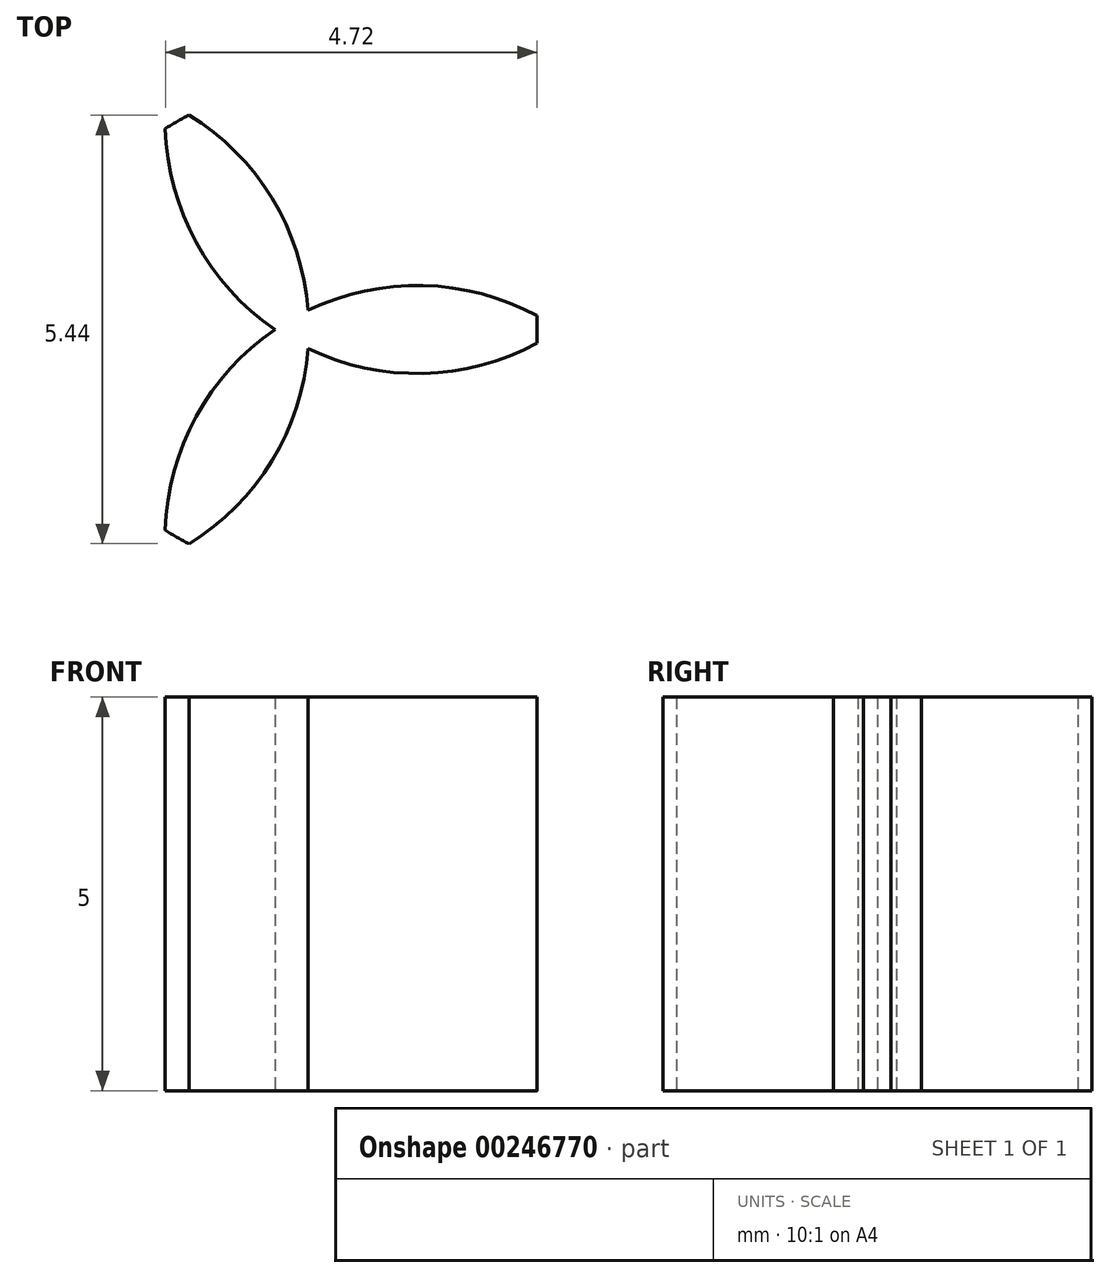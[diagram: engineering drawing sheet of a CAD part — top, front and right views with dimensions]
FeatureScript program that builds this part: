
annotation { "Feature Type Name" : "Feature", "Feature Type Description" : "" }
export const myFeature = defineFeature(function(context is Context, id is Id, definition is map)
    precondition{}
    {
        {
            var Q0;
            Q0=qCreatedBy(makeId("Top.planeOp"),FACE);
            var sketch = newSketch(context, id + "F0", { "sketchPlane" : qUnion([Q0])});
            skCircle(sketch, "E0", {"center": v(0, 0) * mm, "radius": 3.05 * mm});
            skArc(sketch, "E1.cCircle", {"start": v(-1.37, -2.72) * mm, "mid": v(3.05, 0) * mm, "end": v(-1.37, 2.72) * mm, "construction": true});
            skCircle(sketch, "E2", {"center": v(-3.05, 0) * mm, "radius": 3.2 * mm});
            skCircle(sketch, "E3.1.0", {"center": v(1.52, -2.64) * mm, "radius": 3.2 * mm});
            skCircle(sketch, "E3.2.0", {"center": v(1.53, 2.64) * mm, "radius": 3.2 * mm});
            skPoint(sketch, "E1.0.start.orphan", {"position": v(3.05, 0) * mm});
            skSolve(sketch);
        }
        {
            var Q0;
            {var subQ0=sQuery(id+"F0.wireOp",EDGE,"E2");var subQ1=sQuery(id+"F0.wireOp",EDGE,"E0");var subQ2=makeQuery(id+"F0.imprint","INTERSECT",VERTEX,{"disambiguationData":[OD(0.0)],"derivedFrom":[subQ1,subQ0]});Q0=makeQuery(id+"F0.imprint","IMPRINT",FACE,{"disambiguationData":[TD([[makeQuery(id+"F0.imprint","IMPRINT",EDGE,{"disambiguationData":[TD([[subQ2,-1.0]])],"derivedFrom":subQ1}),1.0]])]});}
            var Q1;
            {var subQ0=sQuery(id+"F0.wireOp",EDGE,"E3.1.0");var subQ1=sQuery(id+"F0.wireOp",EDGE,"E0");var subQ2=makeQuery(id+"F0.imprint","INTERSECT",VERTEX,{"disambiguationData":[OD(1.0)],"derivedFrom":[subQ1,subQ0]});Q1=makeQuery(id+"F0.imprint","IMPRINT",FACE,{"disambiguationData":[TD([[makeQuery(id+"F0.imprint","IMPRINT",EDGE,{"disambiguationData":[TD([[subQ2,-1.0]])],"derivedFrom":subQ1}),1.0]])]});}
            var Q2;
            {var subQ0=sQuery(id+"F0.wireOp",EDGE,"E3.1.0");var subQ1=sQuery(id+"F0.wireOp",EDGE,"E0");var subQ2=makeQuery(id+"F0.imprint","INTERSECT",VERTEX,{"disambiguationData":[OD(0.0)],"derivedFrom":[subQ1,subQ0]});Q2=makeQuery(id+"F0.imprint","IMPRINT",FACE,{"disambiguationData":[TD([[makeQuery(id+"F0.imprint","IMPRINT",EDGE,{"disambiguationData":[TD([[subQ2,1.0]])],"derivedFrom":subQ1}),1.0]])]});}
            var Q3;
            {var subQ0=sQuery(id+"F0.wireOp",EDGE,"E3.1.0");var subQ1=sQuery(id+"F0.wireOp",EDGE,"E2");var subQ2=makeQuery(id+"F0.imprint","INTERSECT",VERTEX,{"disambiguationData":[OD(1.0)],"derivedFrom":[subQ1,subQ0]});Q3=makeQuery(id+"F0.imprint","IMPRINT",FACE,{"disambiguationData":[TD([[makeQuery(id+"F0.imprint","IMPRINT",EDGE,{"disambiguationData":[TD([[subQ2,1.0]])],"derivedFrom":subQ1}),1.0]])]});}
            extrude(context, id + "F1", {"entities" : qUnion([Q0, Q1, Q2, Q3]), "depth" : 5 * mm});
        }
    });
